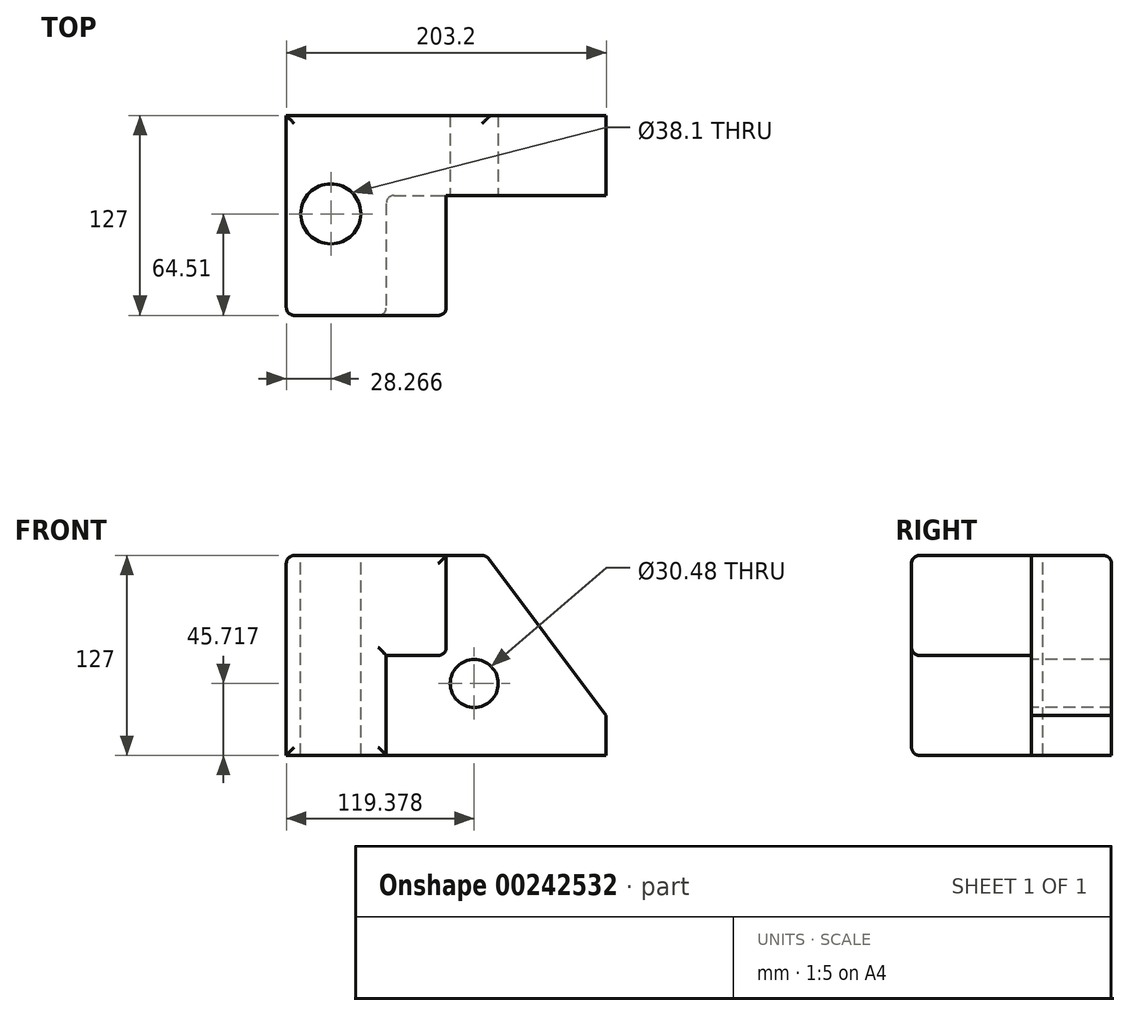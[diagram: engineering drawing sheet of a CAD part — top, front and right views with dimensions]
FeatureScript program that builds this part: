
annotation { "Feature Type Name" : "Feature", "Feature Type Description" : "" }
export const myFeature = defineFeature(function(context is Context, id is Id, definition is map)
    precondition{}
    {
        {
            var Q0;
            Q0=qCreatedBy(makeId("Front.planeOp"),FACE);
            var sketch = newSketch(context, id + "F0", { "sketchPlane" : qUnion([Q0])});
            skLineSegment(sketch, "E0.bottom", {"start": v(-110.31, 80.54) * mm, "end": v(92.89, 80.54) * mm});
            skLineSegment(sketch, "E0.top", {"start": v(-110.31, -46.46) * mm, "end": v(92.89, -46.46) * mm});
            skLineSegment(sketch, "E0.left", {"start": v(-110.31, 80.54) * mm, "end": v(-110.31, -46.46) * mm});
            skLineSegment(sketch, "E0.right", {"start": v(92.89, 80.54) * mm, "end": v(92.89, -46.46) * mm});
            skSolve(sketch);
        }
        {
            var Q0;
            Q0 = qSketchRegion(id + "F0", true);
            extrude(context, id + "F1", {"entities" : qUnion([Q0]), "depth" : 127 * mm});
        }
        {
            var Q0;
            Q0=makeQuery(id+"F1.opExtrude","CAP_FACE",FACE,{"disambiguationData":[OSD([sQuery(id+"F0.wireOp",EDGE,"E0.bottom"),sQuery(id+"F0.wireOp",EDGE,"E0.top"),sQuery(id+"F0.wireOp",EDGE,"E0.left"),sQuery(id+"F0.wireOp",EDGE,"E0.right")])],"isStart":false});
            var sketch = newSketch(context, id + "F2", { "sketchPlane" : qUnion([Q0])});
            skLineSegment(sketch, "E1", {"start": v(-8.71, 80.54) * mm, "end": v(-110.31, 80.54) * mm});
            skLineSegment(sketch, "E2", {"start": v(-110.31, 80.54) * mm, "end": v(-110.31, -46.46) * mm});
            skLineSegment(sketch, "E3", {"start": v(-110.31, -46.46) * mm, "end": v(-46.81, -46.46) * mm});
            skLineSegment(sketch, "E4", {"start": v(-46.81, -46.46) * mm, "end": v(-46.81, 17.04) * mm});
            skLineSegment(sketch, "E5", {"start": v(-46.81, 17.04) * mm, "end": v(-8.71, 17.04) * mm});
            skLineSegment(sketch, "E6", {"start": v(-8.71, 17.04) * mm, "end": v(-8.71, 80.54) * mm});
            skSolve(sketch);
        }
        {
            var Q0;
            {var subQ3=sQuery(id+"F2.wireOp",EDGE,"E4");Q0=makeQuery(id+"F2.imprint","IMPRINT",FACE,{"disambiguationData":[TD([[makeQuery(id+"F2.imprint","IMPRINT",EDGE,{"derivedFrom":subQ3}),-1.0]])]});}
            extrude(context, id + "F3", {"entities" : qUnion([Q0]), "operationType" : NewBodyOperationType.REMOVE, "oppositeDirection" : true, "depth" : 76.2 * mm});
        }
        {
            var Q0;
            Q0=makeQuery(id+"F1.opExtrude","SWEPT_EDGE",EDGE,{"disambiguationData":[OSD([sQuery(id+"F0.wireOp",EDGE,"E0.bottom"),sQuery(id+"F0.wireOp",EDGE,"E0.right")])]});
            chamfer(context, id + "F4", {"entities" : qUnion([Q0]), "chamferType" : ChamferType.TWO_OFFSETS, "width1" : 76.2 * mm, "oppositeDirection" : false, "width2" : 101.6 * mm, "tangentPropagation" : true});
        }
        {
            var Q0;
            Q0=makeQuery(id+"F3.boolean.opBoolean","COPY",EDGE,{"derivedFrom":makeQuery(id+"F3.opExtrude","SWEPT_EDGE",EDGE,{"disambiguationData":[OSD([sQuery(id+"F0.wireOp",EDGE,"E0.bottom"),sQuery(id+"F2.wireOp",EDGE,"E1"),sQuery(id+"F2.wireOp",EDGE,"E6")])]})});
            var Q1;
            Q1=makeQuery(id+"F3.boolean.opBoolean","COPY",EDGE,{"derivedFrom":makeQuery(id+"F3.opExtrude","CAP_EDGE",EDGE,{"disambiguationData":[OSD([sQuery(id+"F0.wireOp",EDGE,"E0.bottom")])],"isStart":false})});
            var Q2;
            Q2=makeQuery(id+"F3.boolean.opBoolean","COPY",EDGE,{"derivedFrom":makeQuery(id+"F3.opExtrude","SWEPT_EDGE",EDGE,{"disambiguationData":[OSD([sQuery(id+"F2.wireOp",EDGE,"E5"),sQuery(id+"F2.wireOp",EDGE,"E6")])]})});
            var Q3;
            Q3=makeQuery(id+"F3.boolean.opBoolean","COPY",EDGE,{"derivedFrom":makeQuery(id+"F3.opExtrude","CAP_EDGE",EDGE,{"disambiguationData":[OSD([sQuery(id+"F2.wireOp",EDGE,"E6")])],"isStart":true})});
            var Q4;
            Q4=makeQuery(id+"F1.opExtrude","CAP_FACE",FACE,{"disambiguationData":[OSD([sQuery(id+"F0.wireOp",EDGE,"E0.bottom"),sQuery(id+"F0.wireOp",EDGE,"E0.top"),sQuery(id+"F0.wireOp",EDGE,"E0.left"),sQuery(id+"F0.wireOp",EDGE,"E0.right")])],"isStart":false});
            var Q5;
            Q5=makeQuery(id+"F3.boolean.opBoolean","COPY",EDGE,{"derivedFrom":makeQuery(id+"F3.opExtrude","CAP_EDGE",EDGE,{"disambiguationData":[OSD([sQuery(id+"F2.wireOp",EDGE,"E4")])],"isStart":false})});
            var Q6;
            {var subQ0=sQuery(id+"F0.wireOp",EDGE,"E0.bottom");Q6=makeQuery(id+"F4.opChamfer","BLEND_EDGE",EDGE,{"blendedFrom":[makeQuery(id+"F1.opExtrude","SWEPT_EDGE",EDGE,{"disambiguationData":[OSD([subQ0,sQuery(id+"F0.wireOp",EDGE,"E0.right")])]}),makeQuery(id+"F1.opExtrude","SWEPT_FACE",FACE,{"disambiguationData":[OSD([subQ0])]})],"blendedInto":[makeQuery(id+"F1.opExtrude","SWEPT_FACE",FACE,{"disambiguationData":[OSD([subQ0])]})]});}
            var Q7;
            Q7=makeQuery(id+"F1.opExtrude","CAP_EDGE",EDGE,{"disambiguationData":[OSD([sQuery(id+"F0.wireOp",EDGE,"E0.bottom")])],"isStart":true});
            var Q8;
            Q8=makeQuery(id+"F1.opExtrude","SWEPT_EDGE",EDGE,{"disambiguationData":[OSD([sQuery(id+"F0.wireOp",EDGE,"E0.bottom"),sQuery(id+"F0.wireOp",EDGE,"E0.left")])]});
            fillet(context, id + "F5", {"entities" : qUnion([Q0, Q1, Q2, Q3, Q4, Q5, Q6, Q7, Q8]), "radius" : 5.08 * mm, "tangentPropagation" : true, "allowEdgeOverflow" : false});
        }
        {
            var Q0;
            Q0=makeQuery(id+"F3.boolean.opBoolean","COPY",FACE,{"derivedFrom":makeQuery(id+"F3.opExtrude","CAP_FACE",FACE,{"disambiguationData":[OSD([sQuery(id+"F0.wireOp",EDGE,"E0.bottom"),sQuery(id+"F0.wireOp",EDGE,"E0.top"),sQuery(id+"F0.wireOp",EDGE,"E0.right"),sQuery(id+"F2.wireOp",EDGE,"E4"),sQuery(id+"F2.wireOp",EDGE,"E5"),sQuery(id+"F2.wireOp",EDGE,"E6")])],"isStart":false})});
            var sketch = newSketch(context, id + "F6", { "sketchPlane" : qUnion([Q0])});
            skCircle(sketch, "E7", {"center": v(9.07, -0.74) * mm, "radius": 15.24 * mm});
            skSolve(sketch);
        }
        {
            var Q0;
            Q0=makeQuery(id+"F6.imprint","IMPRINT",FACE,{"disambiguationData":[TD([[makeQuery(id+"F6.imprint","IMPRINT",EDGE,{"derivedFrom":sQuery(id+"F6.wireOp",EDGE,"E7")}),1.0]])]});
            var Q1;
            Q1=makeQuery(id+"F1.opExtrude","CAP_FACE",FACE,{"disambiguationData":[OSD([sQuery(id+"F0.wireOp",EDGE,"E0.bottom"),sQuery(id+"F0.wireOp",EDGE,"E0.top"),sQuery(id+"F0.wireOp",EDGE,"E0.left"),sQuery(id+"F0.wireOp",EDGE,"E0.right")])],"isStart":true});
            extrude(context, id + "F7", {"entities" : qUnion([Q0]), "operationType" : NewBodyOperationType.REMOVE, "endBound" : BoundingType.UP_TO_SURFACE, "oppositeDirection" : true, "endBoundEntityFace" : qUnion([Q1]), "depth" : 25.4 * mm});
        }
        {
            var Q0;
            Q0=makeQuery(id+"F1.opExtrude","SWEPT_FACE",FACE,{"disambiguationData":[OSD([sQuery(id+"F0.wireOp",EDGE,"E0.bottom")])]});
            var sketch = newSketch(context, id + "F8", { "sketchPlane" : qUnion([Q0])});
            skCircle(sketch, "E8", {"center": v(-82.04, -62.5) * mm, "radius": 19.05 * mm});
            skSolve(sketch);
        }
        {
            var Q0;
            Q0=makeQuery(id+"F8.imprint","IMPRINT",FACE,{"disambiguationData":[TD([[makeQuery(id+"F8.imprint","IMPRINT",EDGE,{"derivedFrom":sQuery(id+"F8.wireOp",EDGE,"E8")}),1.0]])]});
            var Q1;
            Q1=makeQuery(id+"F1.opExtrude","SWEPT_FACE",FACE,{"disambiguationData":[OSD([sQuery(id+"F0.wireOp",EDGE,"E0.top")])]});
            extrude(context, id + "F9", {"entities" : qUnion([Q0]), "operationType" : NewBodyOperationType.REMOVE, "endBound" : BoundingType.UP_TO_SURFACE, "oppositeDirection" : true, "endBoundEntityFace" : qUnion([Q1]), "depth" : 25.4 * mm});
        }
    });
